# Revit family: LA_Vlak
name_source: partatom
category: Generic Models
units: mm (PartAtom-declared; Revit-internal decimal feet)

## family parameters
Can host rebar = No
Cut with Voids When Loaded = No
Maintain Annotation Orientation = No
Part Type = Normal
Room Calculation Point = No
Round Connector Dimension = Use Diameter
Shared = No

## types (6) — shared parameters
Description = Luifel vlak
Manufacturer = Meilof Riks B.V.
Rad_3 = 3 mm  [stored 0.00984252 ft]
Rad_5 = 5 mm  [stored 0.0164042 ft]
URL = https://www.meilofriks.nl
zero-valued in all types: Default Elevation

## per-type parameters (varying)
| type | Diepte_luifel | Hoogte_rug | Hoogte_voorzijde |
| LA.VL.S500A | 500 mm  [stored 1.64042 ft] | 90 mm  [stored 0.295276 ft] | 30 mm  [stored 0.0984252 ft] |
| LA.VL.S450A | 450 mm  [stored 1.47638 ft] | 90 mm  [stored 0.295276 ft] | 30 mm  [stored 0.0984252 ft] |
| LA.VL.S400A | 400 mm  [stored 1.31234 ft] | 90 mm  [stored 0.295276 ft] | 30 mm  [stored 0.0984252 ft] |
| LA.VL.S400B | 400 mm  [stored 1.31234 ft] | 125 mm  [stored 0.410105 ft] | 60 mm  [stored 0.19685 ft] |
| LA.VL.S450B | 450 mm  [stored 1.47638 ft] | 125 mm  [stored 0.410105 ft] | 60 mm  [stored 0.19685 ft] |
| LA.VL.S500B | 500 mm  [stored 1.64042 ft] | 125 mm  [stored 0.410105 ft] | 60 mm  [stored 0.19685 ft] |

note: column(s) folded — value = type name in every type: Model

note: [stored X ft] marks values corroborated as IEEE doubles in the binary element streams (Revit-internal decimal feet)

## geometry (parser evidence)
native form markers: Sweep x2
no freeform markers — native parametric forms only
